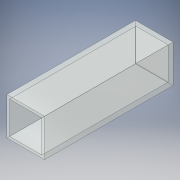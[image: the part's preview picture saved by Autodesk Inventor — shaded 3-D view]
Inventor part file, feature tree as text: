
AUTODESK INVENTOR PART (.ipt)
format: ipt  version: 2019 (Build 230136000, 136)  size: 104,448 bytes
history: native  units: mm
features: extrude x2, sketch x2
ambient origin geometry x8: Origin, YZ Plane, XZ Plane, XY Plane, X Axis, Y Axis, Z Axis, Center Point
bodies: Solid1 (feature_tree)
feature tree (4):
  extrude  "Extrusion1"  Depth=35.0mm
  extrude  "Extrusion2"  Depth=30.0mm
  sketch  "Sketch1"  dims[d0=35.0mm d1=35.0mm]
  sketch  "Sketch2"  dims[d2=30.0mm d3=30.0mm d4=117.5mm d5=0.0mm d6=2.0mm d7=0.0mm]
